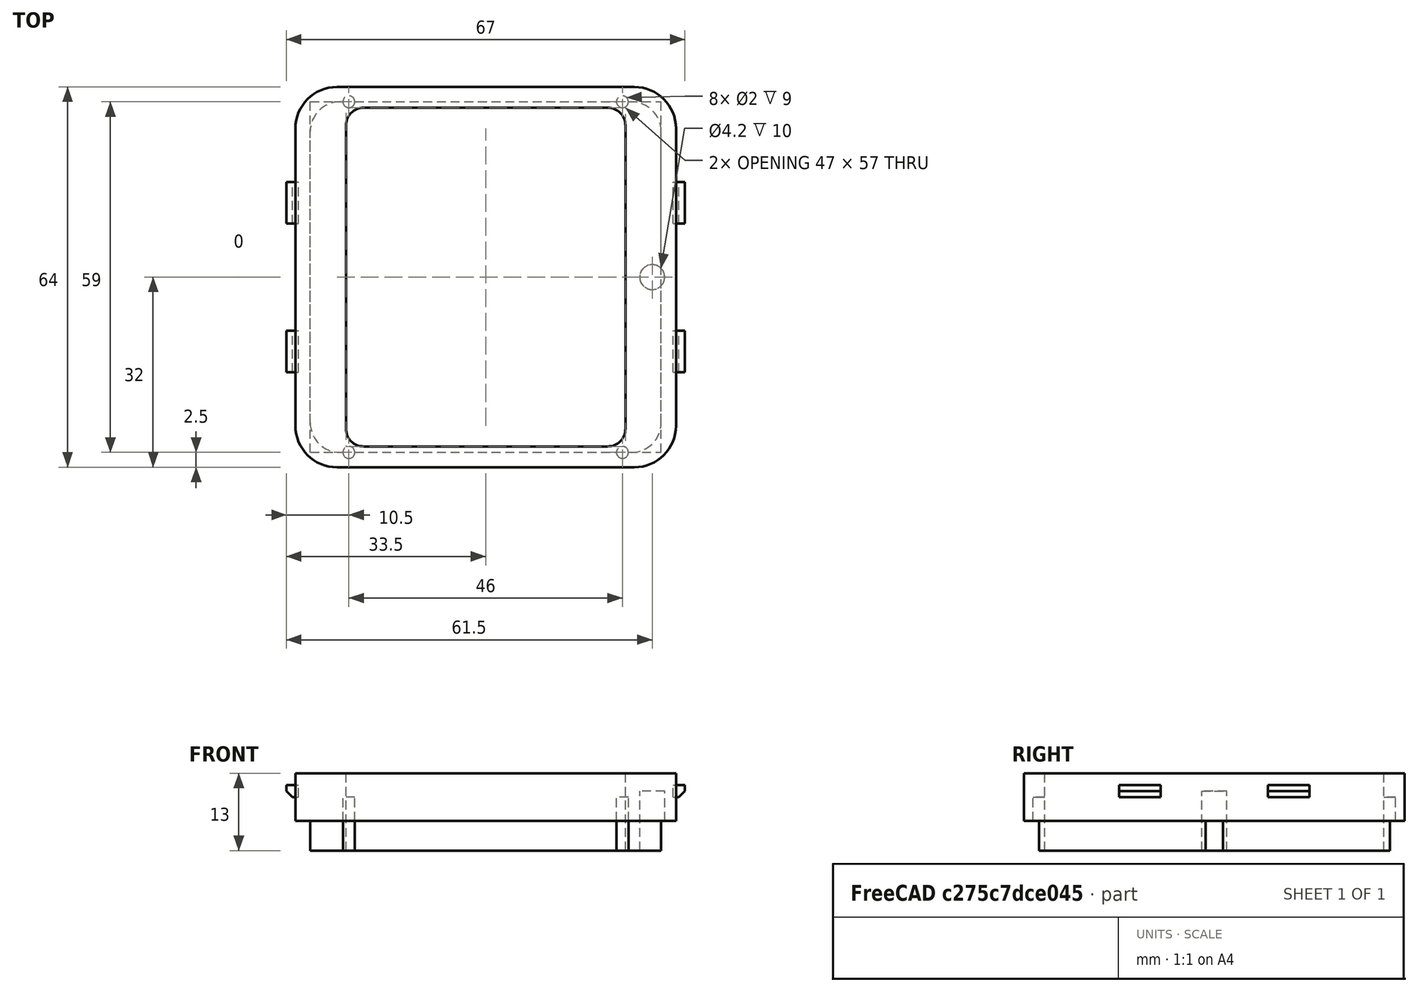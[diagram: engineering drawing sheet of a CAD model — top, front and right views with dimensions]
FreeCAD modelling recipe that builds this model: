
FCSTD DOCUMENT  (FreeCAD 0.16R)
Label: keypad3
License: All rights reserved
LicenseURL: http://en.wikipedia.org/wiki/All_rights_reserved
objects: Part::Cut×10, Part::Box×7, Part::Cylinder×5, Part::Chamfer×4, Part::Fillet×3, Part::MultiFuse×1
note: 30 computed .brp shape members not serialized (recipe doc carries the construction recipe); baked Part::Feature solids carry a one-line shape summary decoded from their .brp

FEATURE [Part::Box] Box  label="Cube"
  Height = 8
  Length = 64
  Placement = pos=(-32,-32,0) rot=(0,0,1;0rad)
  Width = 64
FEATURE [Part::Box] Box001  label="Cube001"
  Height = 5
  Length = 59
  Placement = pos=(-29.5,-29.5,-5) rot=(0,0,1;0rad)
  Width = 59
FEATURE [Part::Box] Box002  label="Cube002"
  Height = 40
  Length = 47
  Placement = pos=(-23.5,-28.5,-20) rot=(0,0,1;0rad)
  Width = 57
FEATURE [Part::MultiFuse] Fusion
  Shapes = -> [Box,Box001]
FEATURE [Part::Cut] Cut
  Base = -> Fusion
  Tool = -> Box002
FEATURE [Part::Box] Box003  label="Cube003"
  Height = 2
  Length = 2
  Placement = pos=(-33.5,9,4) rot=(0,0,1;0rad)
  Width = 7
FEATURE [Part::Box] Box004  label="Cube004"
  Height = 2
  Length = 2
  Placement = pos=(-33.5,-16,4) rot=(0,0,1;0rad)
  Width = 7
FEATURE [Part::Box] Box005  label="Cube005"
  Height = 2
  Length = 2
  Placement = pos=(31.5,-16,4) rot=(0,0,1;0rad)
  Width = 7
FEATURE [Part::Box] Box006  label="Cube006"
  Height = 2
  Length = 2
  Placement = pos=(31.5,9,4) rot=(0,0,1;0rad)
  Width = 7
FEATURE [Part::Cylinder] Cylinder
  Angle = 360
  Height = 27
  Placement = pos=(23,29.5,-23) rot=(0,0,1;0rad)
  Radius = 1
FEATURE [Part::Cylinder] Cylinder001
  Angle = 360
  Height = 27
  Placement = pos=(-23,29.5,-23) rot=(0,0,1;0rad)
  Radius = 1
FEATURE [Part::Cylinder] Cylinder002
  Angle = 360
  Height = 27
  Placement = pos=(-23,-29.5,-23) rot=(0,0,1;0rad)
  Radius = 1
FEATURE [Part::Cylinder] Cylinder003
  Angle = 360
  Height = 27
  Placement = pos=(23,-29.5,-23) rot=(0,0,1;0rad)
  Radius = 1
FEATURE [Part::Fillet] Fillet
  Base = -> Cut
  Edges = 4 edges r=7: [Edge1,Edge3,Edge6,Edge15]
FEATURE [Part::Fillet] Fillet001
  Base = -> Fillet
  Edges = 4 edges r=3: [Edge33,Edge34,Edge36,Edge38]
FEATURE [Part::Fillet] Fillet002
  Base = -> Fillet001
  Edges = 4 edges r=5: [Edge57,Edge58,Edge59,Edge60]
FEATURE [Part::Chamfer] Chamfer
  Base = -> Box003
  Edges = 1 edges r=1: [Edge4]
FEATURE [Part::Chamfer] Chamfer001
  Base = -> Box004
  Edges = 1 edges r=1: [Edge4]
FEATURE [Part::Chamfer] Chamfer002
  Base = -> Box005
  Edges = 1 edges r=1: [Edge8]
FEATURE [Part::Chamfer] Chamfer003
  Base = -> Box006
  Edges = 1 edges r=1: [Edge8]
FEATURE [Part::Cut] Cut001
  Base = -> Fillet001
  Tool = -> Cylinder001
FEATURE [Part::Cut] Cut002
  Base = -> Cut001
  Tool = -> Cylinder
FEATURE [Part::Cut] Cut003
  Base = -> Cut002
  Tool = -> Cylinder002
FEATURE [Part::Cut] Cut004
  Base = -> Cut003
  Tool = -> Cylinder003
FEATURE [Part::Cut] Cut005
  Base = -> Fillet002
  Tool = -> Cylinder001
FEATURE [Part::Cut] Cut006
  Base = -> Cut005
  Tool = -> Cylinder
FEATURE [Part::Cut] Cut007
  Base = -> Cut006
  Tool = -> Cylinder002
FEATURE [Part::Cut] Cut008
  Base = -> Cut007
  Tool = -> Cylinder003
FEATURE [Part::Cylinder] Cylinder004
  Angle = 360
  Height = 20
  Placement = pos=(28,0,-15) rot=(0,0,1;0rad)
  Radius = 2.1
FEATURE [Part::Cut] Cut009
  Base = -> Cut008
  Tool = -> Cylinder004
